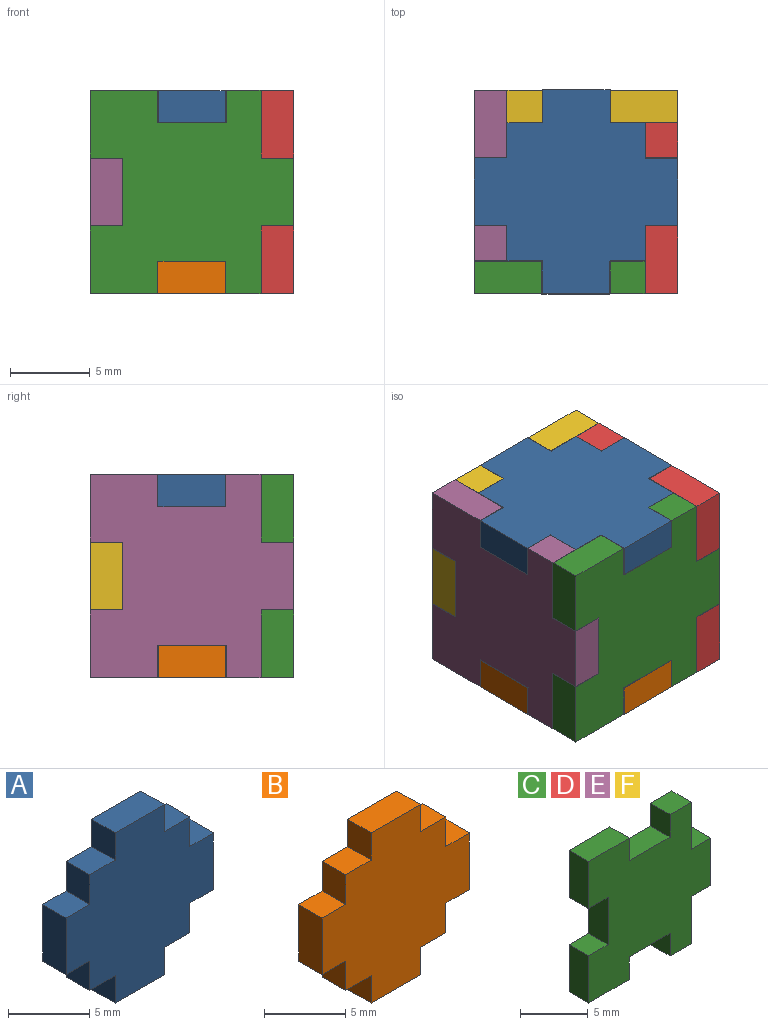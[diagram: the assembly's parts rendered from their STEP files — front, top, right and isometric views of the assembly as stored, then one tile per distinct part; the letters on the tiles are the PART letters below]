
ASSEMBLY  parts=6 mates=5
PART A: 22 faces, bbox 12.8x2x12.8 mm
  f0: plane 2.04x2.03mm, normal (0,0,-1), area 4.2mm2, adj f1,f19,f20,f21
  f1: plane 4.25x2.03mm, normal (1,0,0), area 8.6mm2, adj f0,f2,f20,f21
  f2: plane 2.04x2.03mm, normal (0,0,1), area 4.2mm2, adj f1,f3,f20,f21
  f3: plane 2.22x2.03mm, normal (1,0,0), area 4.5mm2, adj f2,f4,f20,f21
  f4: plane 2.22x2.03mm, normal (0,0,1), area 4.5mm2, adj f3,f5,f20,f21
  f5: plane 2.04x2.03mm, normal (1,0,0), area 4.2mm2, adj f4,f6,f20,f21
  f6: plane 4.25x2.03mm, normal (0,0,1), area 8.6mm2, adj f5,f7,f20,f21
  f7: plane 2.04x2.03mm, normal (-1,0,0), area 4.2mm2, adj f6,f8,f20,f21
  f8: plane 2.22x2.03mm, normal (0,0,1), area 4.5mm2, adj f7,f9,f20,f21
  f9: plane 2.22x2.03mm, normal (-1,0,0), area 4.5mm2, adj f8,f10,f20,f21
  f10: plane 2.04x2.03mm, normal (0,0,1), area 4.2mm2, adj f9,f11,f20,f21
  f11: plane 4.25x2.03mm, normal (-1,0,0), area 8.6mm2, adj f10,f12,f20,f21
  f12: plane 2.04x2.03mm, normal (0,0,-1), area 4.2mm2, adj f11,f13,f20,f21
  f13: plane 2.22x2.03mm, normal (-1,0,0), area 4.5mm2, adj f12,f14,f20,f21
  f14: plane 2.22x2.03mm, normal (0,0,-1), area 4.5mm2, adj f13,f15,f20,f21
  f15: plane 2.04x2.03mm, normal (-1,0,0), area 4.2mm2, adj f14,f16,f20,f21
  f16: plane 4.25x2.03mm, normal (0,0,-1), area 8.6mm2, adj f15,f17,f20,f21
  f17: plane 2.04x2.03mm, normal (1,0,0), area 4.2mm2, adj f16,f18,f20,f21
  f18: plane 2.22x2.03mm, normal (0,0,-1), area 4.5mm2, adj f17,f19,f20,f21
  f19: plane 2.22x2.03mm, normal (1,0,0), area 4.5mm2, adj f0,f18,f20,f21
  f20: plane 12.79x12.79mm, normal (0,-1,0), area 110.5mm2, adj f0,f1,f2,f3,f4,f5,f6,f7
  f21: plane 12.79x12.79mm, normal (0,1,0), area 110.5mm2, adj f0,f1,f2,f3,f4,f5,f6,f7
PART B: 37 faces, bbox 12.8x2x12.8 mm
  f0: plane 2.04x2.03mm, normal (0,0,-1), area 4.2mm2, adj f1,f19,f20,f21
  f1: plane 4.25x2.03mm, normal (1,0,0), area 8.6mm2, adj f0,f2,f20,f21
  f2: plane 2.04x2.03mm, normal (0,0,1), area 4.2mm2, adj f1,f3,f20,f21
  f3: plane 2.22x2.03mm, normal (1,0,0), area 4.5mm2, adj f2,f4,f20,f21
  f4: plane 2.22x2.03mm, normal (0,0,1), area 4.5mm2, adj f3,f5,f20,f21
  f5: plane 2.04x2.03mm, normal (1,0,0), area 4.2mm2, adj f4,f6,f20,f21
  f6: plane 4.25x2.03mm, normal (0,0,1), area 8.6mm2, adj f5,f7,f20,f21
  f7: plane 2.04x2.03mm, normal (-1,0,0), area 4.2mm2, adj f6,f8,f20,f21
  f8: plane 2.22x2.03mm, normal (0,0,1), area 4.5mm2, adj f7,f9,f20,f21
  f9: plane 2.22x2.03mm, normal (-1,0,0), area 4.5mm2, adj f8,f10,f20,f21
  f10: plane 2.04x2.03mm, normal (0,0,1), area 4.2mm2, adj f9,f11,f20,f21
  f11: plane 4.25x2.03mm, normal (-1,0,0), area 8.6mm2, adj f10,f12,f20,f21
  f12: plane 2.04x2.03mm, normal (0,0,-1), area 4.2mm2, adj f11,f13,f20,f21
  f13: plane 2.22x2.03mm, normal (-1,0,0), area 4.5mm2, adj f12,f14,f20,f21
  f14: plane 2.22x2.03mm, normal (0,0,-1), area 4.5mm2, adj f13,f15,f20,f21
  f15: plane 2.04x2.03mm, normal (-1,0,0), area 4.2mm2, adj f14,f16,f20,f21
  f16: plane 4.25x2.03mm, normal (0,0,-1), area 8.6mm2, adj f15,f17,f20,f21
  f17: plane 2.04x2.03mm, normal (1,0,0), area 4.2mm2, adj f16,f18,f20,f21
  f18: plane 2.22x2.03mm, normal (0,0,-1), area 4.5mm2, adj f17,f19,f20,f21
  f19: plane 2.22x2.03mm, normal (1,0,0), area 4.5mm2, adj f0,f18,f20,f21
  f20: plane 12.79x12.79mm, normal (0,-1,0), area 110.5mm2, adj f0,f1,f2,f3,f4,f5,f6,f7
  f21: plane 12.79x12.79mm, normal (0,1,0), area 95.7mm2, adj f0,f1,f2,f3,f4,f5,f6,f7
  f22: plane 0.81x0.51mm, normal (0,0,1), area 0.4mm2, adj f21,f23,f34,f35
  f23: plane 6.74x2.64mm, normal (-0.93,0,-0.36), area 3.7mm2, adj f21,f22,f24,f35
  f24: plane 0.66x0.51mm, normal (0,0,-1), area 0.3mm2, adj f21,f23,f25,f35
  f25: plane 6.74x2.65mm, normal (0.93,0,-0.37), area 3.7mm2, adj f21,f24,f26,f35
  f26: plane 0.79x0.51mm, normal (0,0,1), area 0.4mm2, adj f21,f25,f27,f35
  f27: plane 2.13x0.83mm, normal (-0.93,0,0.36), area 1.2mm2, adj f21,f26,f28,f35
  f28: plane 2.69x0.51mm, normal (0,0,1), area 1.4mm2, adj f21,f27,f34,f35
  f29: plane 2.17x0.51mm, normal (0,0,-1), area 1.1mm2, adj f30,f33,f35,f36
  f30: plane 2.08x0.79mm, normal (-0.94,0,0.35), area 1.1mm2, adj f29,f31,f35,f36
  f31: extruded ~0.97x0.51mm, area 0.5mm2, adj f30,f32,f35,f36
  f32: extruded ~0.97x0.51mm, area 0.5mm2, adj f31,f33,f35,f36
  f33: plane 2.08x0.78mm, normal (0.94,0,0.35), area 1.1mm2, adj f29,f32,f35,f36
  f34: plane 2.13x0.84mm, normal (0.93,0,0.36), area 1.2mm2, adj f21,f22,f28,f35
  f35: plane 6.74x5.95mm, normal (0,1,0), area 11.6mm2, adj f22,f23,f24,f25,f26,f27,f28,f29
  f36: plane 3.05x2.17mm, normal (0,1,0), area 3.2mm2, adj f29,f30,f31,f32,f33
PART C: 22 faces, bbox 12.8x2x12.8 mm
  f0: plane 4.27x2.03mm, normal (-1,0,0), area 8.7mm2, adj f1,f19,f20,f21
  f1: plane 2.04x2.03mm, normal (0,0,1), area 4.2mm2, adj f0,f2,f20,f21
  f2: plane 4.25x2.03mm, normal (-1,0,0), area 8.6mm2, adj f1,f3,f20,f21
  f3: plane 4.25x2.03mm, normal (0,0,-1), area 8.6mm2, adj f2,f4,f20,f21
  f4: plane 2.04x2.03mm, normal (1,0,0), area 4.2mm2, adj f3,f5,f20,f21
  f5: plane 4.25x2.03mm, normal (0,0,-1), area 8.6mm2, adj f4,f6,f20,f21
  f6: plane 2.04x2.03mm, normal (-1,0,0), area 4.2mm2, adj f5,f7,f20,f21
  f7: plane 2.22x2.03mm, normal (0,0,-1), area 4.5mm2, adj f6,f8,f20,f21
  f8: plane 4.25x2.03mm, normal (1,0,0), area 8.6mm2, adj f7,f9,f20,f21
  f9: plane 2.04x2.03mm, normal (0,0,-1), area 4.2mm2, adj f8,f10,f20,f21
  f10: plane 4.27x2.03mm, normal (1,0,0), area 8.7mm2, adj f9,f11,f20,f21
  f11: plane 2.04x2.03mm, normal (0,0,1), area 4.2mm2, adj f10,f12,f20,f21
  f12: plane 4.25x2.03mm, normal (1,0,0), area 8.6mm2, adj f11,f13,f20,f21
  f13: plane 2.22x2.03mm, normal (0,0,1), area 4.5mm2, adj f12,f14,f20,f21
  f14: plane 2.04x2.03mm, normal (-1,0,0), area 4.2mm2, adj f13,f15,f20,f21
  f15: plane 4.25x2.03mm, normal (0,0,1), area 8.6mm2, adj f14,f16,f20,f21
  f16: plane 2.04x2.03mm, normal (1,0,0), area 4.2mm2, adj f15,f17,f20,f21
  f17: plane 4.25x2.03mm, normal (0,0,1), area 8.6mm2, adj f16,f18,f20,f21
  f18: plane 4.25x2.03mm, normal (-1,0,0), area 8.6mm2, adj f17,f19,f20,f21
  f19: plane 2.04x2.03mm, normal (0,0,-1), area 4.2mm2, adj f0,f18,f20,f21
  f20: plane 12.78x12.78mm, normal (0,-1,0), area 119.7mm2, adj f0,f1,f2,f3,f4,f5,f6,f7
  f21: plane 12.78x12.78mm, normal (0,1,0), area 119.7mm2, adj f0,f1,f2,f3,f4,f5,f6,f7
PART D: same geometry as C
PART E: same geometry as C
PART F: same geometry as C
PLACE A rot(axis=(0,-0.71,0.71),180deg) t=(-59.51,64.66,45.33)mm
PLACE B rot(axis=(-1,0,0),90deg) t=(-24.84,4.97,34.61)mm
PLACE C t=(-35.53,30.47,14.1)mm
PLACE D rot(axis=(0,0,1),90deg) t=(-37.82,41.46,14.1)mm
PLACE E rot(axis=(0,0,-1),90deg) t=(-46.52,28.18,14.1)mm
PLACE F rot(axis=(0,0,1),180deg) t=(-48.81,39.17,14.1)mm
MATE fastened E.f21 <-> C.f0  axis (1,0,0) through (-46.52,28.43,40.99)mm
MATE fastened B.f20 <-> D.f5  axis (0,0,1) through (-35.79,34.8,36.65)mm
MATE fastened F.f0 <-> D.f21  axis (1,0,0) through (-37.82,41.2,40.99)mm
MATE fastened E.f15 <-> A.f21  axis (0,0,1) through (-48.55,34.83,45.33)mm
MATE fastened C.f21 <-> D.f0  axis (0,1,0) through (-35.79,30.47,40.99)mm
